# Revit family: Geräteeinsätze GES_Geräteeinsatz_GESR7_mit_Griffbügel
name_source: partatom
category: Generic Models
revit_build: Autodesk Revit 2015 (Build: 20140606_1530(x64)
units: mm (PartAtom-declared; Revit-internal decimal feet)

## types (3) — shared parameters
Bodenbelagdicke = 10 mm  [stored 0.0328084 ft]
Diameter dimesion = 274 mm  [stored 0.89895 ft]
Height = 66 mm  [stored 0.216535 ft]
Inner cut = 260 mm  [stored 0.853018 ft]
Inner cut 3 = 234 mm
Manufacturer = OBO Bettermann
Outer Diameter Dimension = 294 mm  [stored 0.964567 ft]
Snur width = 111 mm
URL = http://www.obo-bettermann.com

## per-type parameters (varying)
| type | GTIN | Inner cut2 | Manufacturer Art. No. | Material |
| GESR7 10U 7011 | 4012195103738 | 165 mm | 7405452 | Plastic RAL 7011 |
| GESR7 10U 9011 | 4012195103790 | 166 mm | 7405456 | Plastic RAL 9011 |
| GESR7 10U 1019 | 4012195103806 | 166 mm | 7405460 | Plastic RAL 1019 |

note: column(s) folded — value = type name in every type: Article Type

note: [stored X ft] marks values corroborated as IEEE doubles in the binary element streams (Revit-internal decimal feet)

## geometry (parser evidence)
native form markers: Sweep x2
no freeform markers — native parametric forms only
